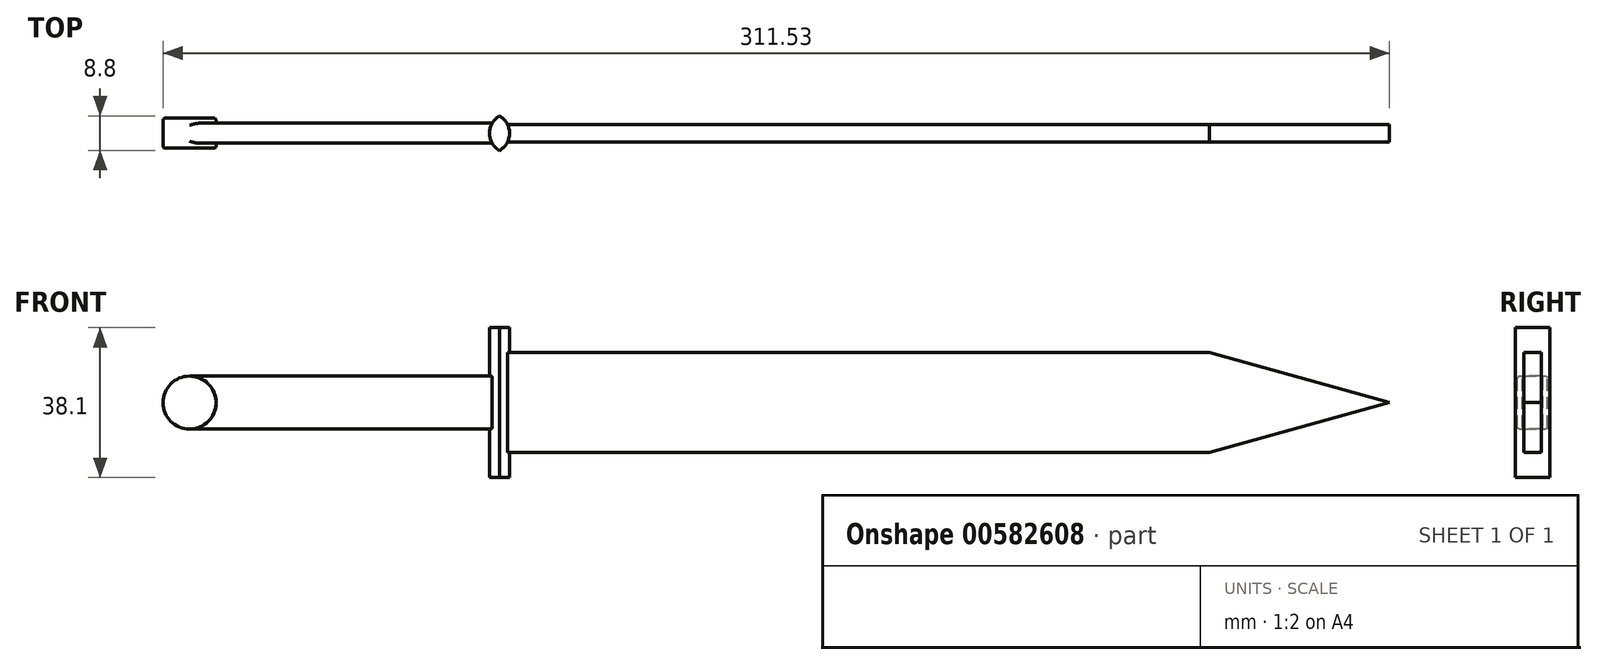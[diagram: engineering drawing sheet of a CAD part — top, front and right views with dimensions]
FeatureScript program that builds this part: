
annotation { "Feature Type Name" : "Feature", "Feature Type Description" : "" }
export const myFeature = defineFeature(function(context is Context, id is Id, definition is map)
    precondition{}
    {
        {
            var Q0;
            Q0=qCreatedBy(makeId("Front.planeOp"),FACE);
            var sketch = newSketch(context, id + "F0", { "sketchPlane" : qUnion([Q0])});
            skCircle(sketch, "E0", {"center": v(-76.2, 0) * mm, "radius": 6.73 * mm});
            skLineSegment(sketch, "E1", {"start": v(-76.2, 6.73) * mm, "end": v(0, 6.73) * mm});
            skLineSegment(sketch, "E2", {"start": v(-76.2, -6.73) * mm, "end": v(0, -6.73) * mm});
            skLineSegment(sketch, "E3", {"start": v(0, 0) * mm, "end": v(0, -19.05) * mm});
            skLineSegment(sketch, "E4", {"start": v(0, 0) * mm, "end": v(0, 19.05) * mm});
            skLineSegment(sketch, "E5", {"start": v(0, 19.05) * mm, "end": v(5.08, 19.05) * mm});
            skLineSegment(sketch, "E6", {"start": v(0, -19.05) * mm, "end": v(5.08, -19.05) * mm});
            skLineSegment(sketch, "E7", {"start": v(5.08, 19.05) * mm, "end": v(5.08, -19.05) * mm});
            skLineSegment(sketch, "E8", {"start": v(5.08, 19.05) * mm, "end": v(5.08, 12.7) * mm, "construction": true});
            skLineSegment(sketch, "E9", {"start": v(5.08, -19.05) * mm, "end": v(5.08, -12.7) * mm, "construction": true});
            skLineSegment(sketch, "E10", {"start": v(5.08, 12.7) * mm, "end": v(182.88, 12.7) * mm});
            skLineSegment(sketch, "E11", {"start": v(5.08, -12.7) * mm, "end": v(182.88, -12.7) * mm});
            skLineSegment(sketch, "E12", {"start": v(0, 0) * mm, "end": v(228.6, 0) * mm, "construction": true});
            skLineSegment(sketch, "E13", {"start": v(182.88, 12.7) * mm, "end": v(228.6, 0) * mm});
            skLineSegment(sketch, "E14", {"start": v(182.88, -12.7) * mm, "end": v(228.6, 0) * mm});
            skSolve(sketch);
        }
        {
            var Q0;
            {var subQ4=sQuery(id+"F0.wireOp",EDGE,"E1");Q0=makeQuery(id+"F0.imprint","IMPRINT",FACE,{"disambiguationData":[TD([[makeQuery(id+"F0.imprint","IMPRINT",EDGE,{"derivedFrom":subQ4}),-1.0]])]});}
            extrude(context, id + "F1", {"entities" : qUnion([Q0]), "depth" : 5.08 * mm, "offsetDistance" : 25.4 * mm, "symmetric" : true});
        }
        {
            var Q0;
            {var subQ0=sQuery(id+"F0.wireOp",EDGE,"E0");var subQ1=makeQuery(id+"F0.imprint","INTERSECT",VERTEX,{"derivedFrom":[subQ0,sQuery(id+"F0.wireOp",EDGE,"E1")]});Q0=makeQuery(id+"F0.imprint","IMPRINT",FACE,{"disambiguationData":[TD([[makeQuery(id+"F0.imprint","IMPRINT",EDGE,{"disambiguationData":[TD([[subQ1,-1.0]])],"derivedFrom":subQ0}),1.0]])]});}
            extrude(context, id + "F2", {"entities" : qUnion([Q0]), "operationType" : NewBodyOperationType.ADD, "depth" : 7.62 * mm, "offsetDistance" : 25.4 * mm, "symmetric" : true});
        }
        {
            var Q0;
            {var subQ2=sQuery(id+"F0.wireOp",EDGE,"E5");Q0=makeQuery(id+"F0.imprint","IMPRINT",FACE,{"disambiguationData":[TD([[makeQuery(id+"F0.imprint","IMPRINT",EDGE,{"derivedFrom":subQ2}),-1.0]])]});}
            extrude(context, id + "F3", {"entities" : qUnion([Q0]), "operationType" : NewBodyOperationType.ADD, "depth" : 10.16 * mm, "offsetDistance" : 25.4 * mm, "symmetric" : true});
        }
        {
            var Q0;
            {var subQ1=sQuery(id+"F0.wireOp",EDGE,"E10");Q0=makeQuery(id+"F0.imprint","IMPRINT",FACE,{"disambiguationData":[TD([[makeQuery(id+"F0.imprint","IMPRINT",EDGE,{"derivedFrom":subQ1}),-1.0]])]});}
            extrude(context, id + "F4", {"entities" : qUnion([Q0]), "operationType" : NewBodyOperationType.ADD, "depth" : 4.44 * mm, "offsetDistance" : 25.4 * mm, "symmetric" : true});
        }
        {
            var Q0;
            Q0=makeQuery(id+"F1.opExtrude","CAP_EDGE",EDGE,{"disambiguationData":[OSD([sQuery(id+"F0.wireOp",EDGE,"E1")])],"isStart":false});
            var Q1;
            Q1=makeQuery(id+"F1.opExtrude","CAP_EDGE",EDGE,{"disambiguationData":[OSD([sQuery(id+"F0.wireOp",EDGE,"E2")])],"isStart":false});
            var Q2;
            Q2=makeQuery(id+"F1.opExtrude","CAP_EDGE",EDGE,{"disambiguationData":[OSD([sQuery(id+"F0.wireOp",EDGE,"E2")])],"isStart":true});
            var Q3;
            Q3=makeQuery(id+"F1.opExtrude","CAP_EDGE",EDGE,{"disambiguationData":[OSD([sQuery(id+"F0.wireOp",EDGE,"E1")])],"isStart":true});
            fillet(context, id + "F5", {"entities" : qUnion([Q0, Q1, Q2, Q3]), "radius" : 0.5 * mm, "tangentPropagation" : true, "allowEdgeOverflow" : false});
        }
        {
            var Q0;
            Q0=makeQuery(id+"F2.opExtrude","CAP_EDGE",EDGE,{"disambiguationData":[OSD([sQuery(id+"F0.wireOp",EDGE,"E0")])],"isStart":false});
            var Q1;
            Q1=makeQuery(id+"F2.opExtrude","CAP_EDGE",EDGE,{"disambiguationData":[OSD([sQuery(id+"F0.wireOp",EDGE,"E0")])],"isStart":true});
            fillet(context, id + "F6", {"entities" : qUnion([Q0, Q1]), "radius" : 0.5 * mm, "tangentPropagation" : true, "allowEdgeOverflow" : false});
        }
        {
            var Q0;
            Q0=makeQuery(id+"F3.opExtrude","CAP_EDGE",EDGE,{"disambiguationData":[OSD([sQuery(id+"F0.wireOp",EDGE,"E3"),sQuery(id+"F0.wireOp",EDGE,"E4")])],"isStart":false});
            var Q1;
            Q1=makeQuery(id+"F3.opExtrude","CAP_EDGE",EDGE,{"disambiguationData":[OSD([sQuery(id+"F0.wireOp",EDGE,"E7")])],"isStart":false});
            var Q2;
            Q2=makeQuery(id+"F3.opExtrude","CAP_EDGE",EDGE,{"disambiguationData":[OSD([sQuery(id+"F0.wireOp",EDGE,"E3"),sQuery(id+"F0.wireOp",EDGE,"E4")])],"isStart":true});
            var Q3;
            Q3=makeQuery(id+"F3.opExtrude","CAP_EDGE",EDGE,{"disambiguationData":[OSD([sQuery(id+"F0.wireOp",EDGE,"E7")])],"isStart":true});
            fillet(context, id + "F7", {"entities" : qUnion([Q0, Q1, Q2, Q3]), "radius" : 5.08 * mm, "tangentPropagation" : true, "allowEdgeOverflow" : false});
        }
    });
